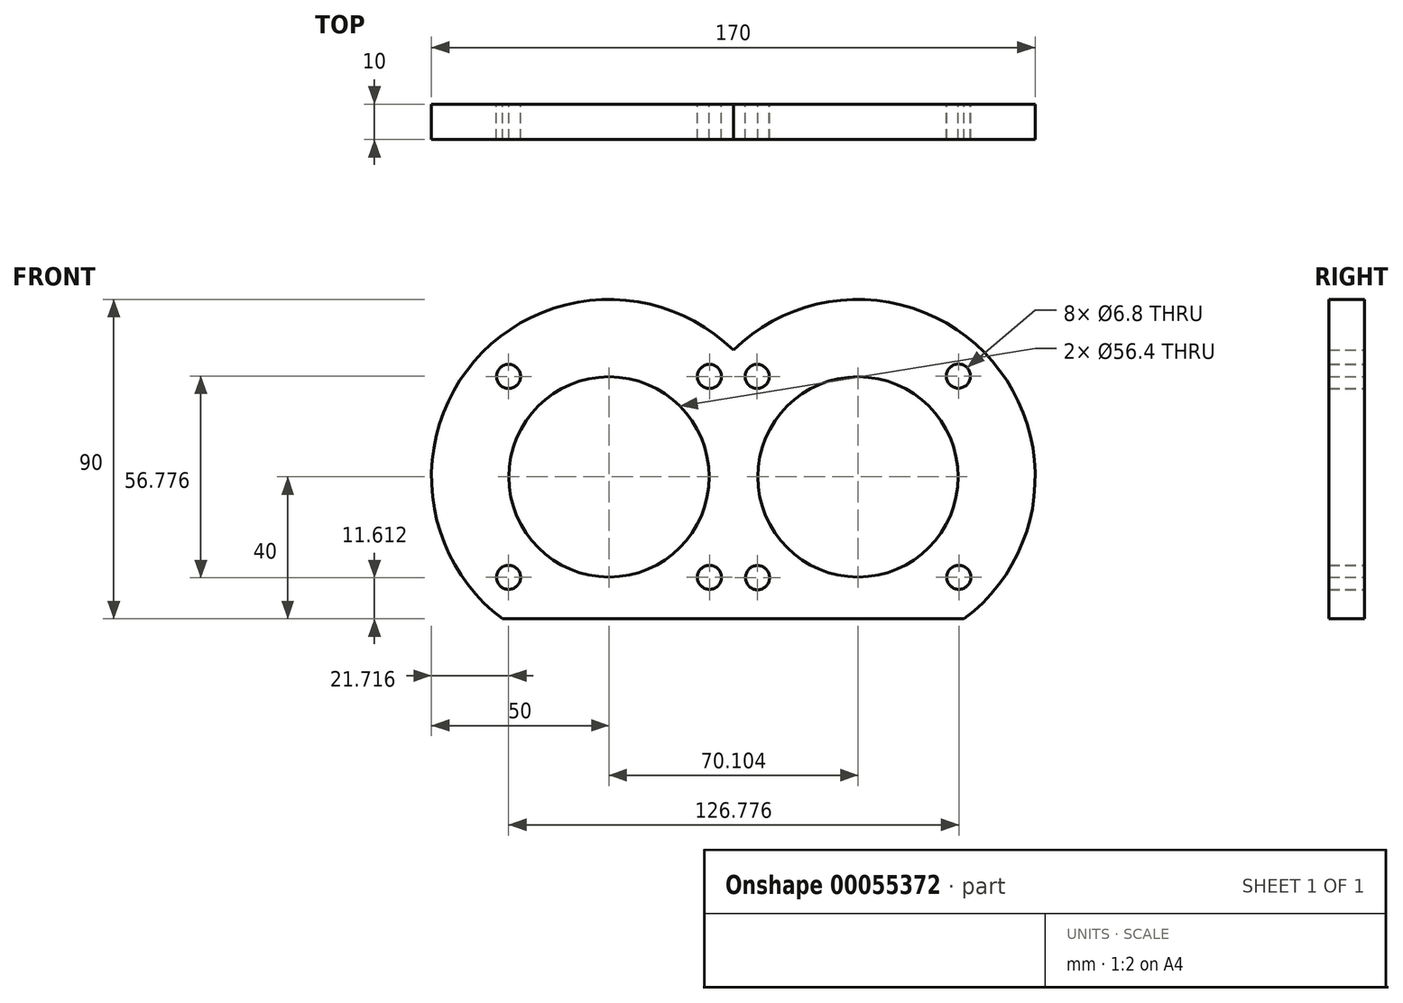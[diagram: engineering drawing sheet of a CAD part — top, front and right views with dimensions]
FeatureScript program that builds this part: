
annotation { "Feature Type Name" : "Feature", "Feature Type Description" : "" }
export const myFeature = defineFeature(function(context is Context, id is Id, definition is map)
    precondition{}
    {
        {
            var Q0;
            Q0=qCreatedBy(makeId("Front.planeOp"),FACE);
            var sketch = newSketch(context, id + "F0", { "sketchPlane" : qUnion([Q0])});
            skCircle(sketch, "E0", {"center": v(-35, 0) * mm, "radius": 28.2 * mm});
            skArc(sketch, "E1", {"start": v(0, 35.7) * mm, "mid": v(-72.94, 32.57) * mm, "end": v(-65, -40) * mm});
            skArc(sketch, "E2.trimOffspring", {"start": v(65, -40) * mm, "mid": v(72.94, 32.57) * mm, "end": v(0, 35.7) * mm});
            skCircle(sketch, "E3", {"center": v(35.1, 0) * mm, "radius": 28.2 * mm});
            skCircle(sketch, "E4.1.0", {"center": v(-63.28, 28.28) * mm, "radius": 3.4 * mm});
            skCircle(sketch, "E4.3.0", {"center": v(-63.28, -28.28) * mm, "radius": 3.4 * mm});
            skCircle(sketch, "E4.5.0", {"center": v(-6.72, -28.28) * mm, "radius": 3.4 * mm});
            skCircle(sketch, "E4.7.0", {"center": v(-6.72, 28.28) * mm, "radius": 3.4 * mm});
            skCircle(sketch, "E5.1.0", {"center": v(6.72, 28.28) * mm, "radius": 3.4 * mm});
            skCircle(sketch, "E6.1.3.0", {"center": v(6.82, -28.39) * mm, "radius": 3.4 * mm});
            skCircle(sketch, "E6.1.5.0", {"center": v(63.5, -28.28) * mm, "radius": 3.4 * mm});
            skCircle(sketch, "E6.1.7.0", {"center": v(63.39, 28.39) * mm, "radius": 3.4 * mm});
            skLineSegment(sketch, "E7.0", {"start": v(-65, -40) * mm, "end": v(65, -40) * mm});
            skSolve(sketch);
        }
        {
            var Q0;
            Q0=makeQuery(id+"F0.imprint","IMPRINT",FACE,{"disambiguationData":[TD([[makeQuery(id+"F0.imprint","IMPRINT",EDGE,{"derivedFrom":sQuery(id+"F0.wireOp",EDGE,"E0")}),-1.0]])]});
            var Q1;
            Q1=makeQuery(id+"F0.imprint","IMPRINT",FACE,{"disambiguationData":[TD([[makeQuery(id+"F0.imprint","IMPRINT",EDGE,{"derivedFrom":sQuery(id+"F0.wireOp",EDGE,"E2.trimOffspring")}),1.0]])]});
            extrude(context, id + "F1", {"entities" : qUnion([Q0, Q1]), "depth" : 10 * mm});
        }
    });
